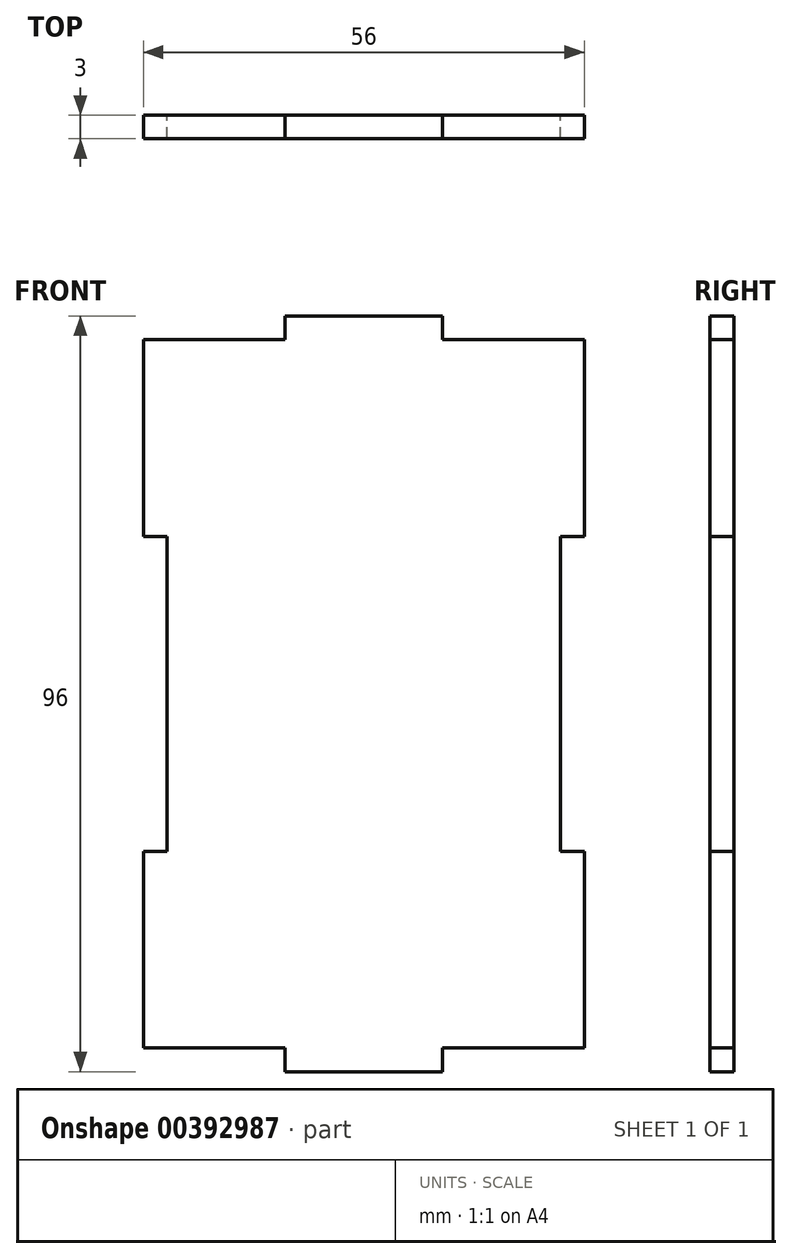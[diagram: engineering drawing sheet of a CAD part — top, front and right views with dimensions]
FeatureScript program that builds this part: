
annotation { "Feature Type Name" : "Feature", "Feature Type Description" : "" }
export const myFeature = defineFeature(function(context is Context, id is Id, definition is map)
    precondition{}
    {
        {
            var Q0;
            Q0=qCreatedBy(makeId("Front.planeOp"),FACE);
            var sketch = newSketch(context, id + "F0", { "sketchPlane" : qUnion([Q0])});
            skLineSegment(sketch, "E0", {"start": v(0, 48) * mm, "end": v(-10, 48) * mm});
            skLineSegment(sketch, "E1", {"start": v(-10, 48) * mm, "end": v(-10, 45) * mm});
            skLineSegment(sketch, "E2", {"start": v(-10, 45) * mm, "end": v(-28, 45) * mm});
            skLineSegment(sketch, "E3", {"start": v(-28, 45) * mm, "end": v(-28, 20) * mm});
            skLineSegment(sketch, "E4", {"start": v(-28, 20) * mm, "end": v(-25, 20) * mm});
            skLineSegment(sketch, "E5", {"start": v(-25, 20) * mm, "end": v(-25, 0) * mm});
            skLineSegment(sketch, "E6.MirrorCS", {"start": v(28, 20) * mm, "end": v(25, 20) * mm});
            skLineSegment(sketch, "E7.MirrorCS", {"start": v(10, 48) * mm, "end": v(10, 45) * mm});
            skLineSegment(sketch, "E8.MirrorCS", {"start": v(25, 20) * mm, "end": v(25, 0) * mm});
            skLineSegment(sketch, "E9.MirrorCS", {"start": v(0, 48) * mm, "end": v(10, 48) * mm});
            skLineSegment(sketch, "E10.MirrorCS", {"start": v(28, 45) * mm, "end": v(28, 20) * mm});
            skLineSegment(sketch, "E11.MirrorCS", {"start": v(10, 45) * mm, "end": v(28, 45) * mm});
            skLineSegment(sketch, "E12.MirrorCS", {"start": v(10, -48) * mm, "end": v(10, -45) * mm});
            skLineSegment(sketch, "E13.MirrorCS", {"start": v(28, -20) * mm, "end": v(25, -20) * mm});
            skLineSegment(sketch, "E14.MirrorCS", {"start": v(-10, -48) * mm, "end": v(-10, -45) * mm});
            skLineSegment(sketch, "E15.MirrorCS", {"start": v(-28, -20) * mm, "end": v(-25, -20) * mm});
            skLineSegment(sketch, "E16.MirrorCS", {"start": v(10, -45) * mm, "end": v(28, -45) * mm});
            skLineSegment(sketch, "E17.MirrorCS", {"start": v(28, -45) * mm, "end": v(28, -20) * mm});
            skLineSegment(sketch, "E18.MirrorCS", {"start": v(0, -48) * mm, "end": v(10, -48) * mm});
            skLineSegment(sketch, "E19.MirrorCS", {"start": v(25, -20) * mm, "end": v(25, 0) * mm});
            skLineSegment(sketch, "E20.MirrorCS", {"start": v(-10, -45) * mm, "end": v(-28, -45) * mm});
            skLineSegment(sketch, "E21.MirrorCS", {"start": v(0, -48) * mm, "end": v(-10, -48) * mm});
            skLineSegment(sketch, "E22.MirrorCS", {"start": v(-25, -20) * mm, "end": v(-25, 0) * mm});
            skLineSegment(sketch, "E23.MirrorCS", {"start": v(-28, -45) * mm, "end": v(-28, -20) * mm});
            skSolve(sketch);
        }
        {
            var Q0;
            Q0=qSketchRegion(id+"F0",true);
            extrude(context, id + "F1", {"entities" : qUnion([Q0]), "depth" : 3 * mm});
        }
    });
